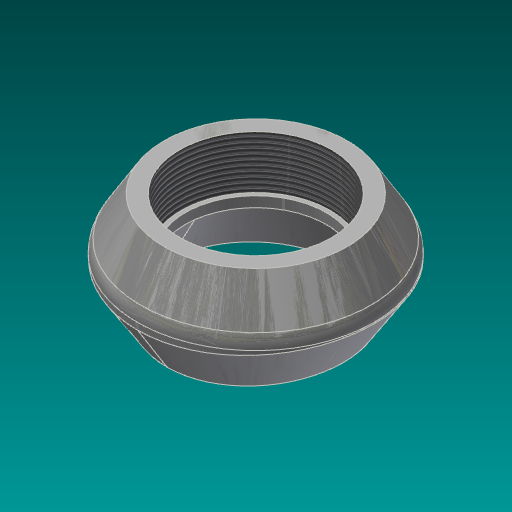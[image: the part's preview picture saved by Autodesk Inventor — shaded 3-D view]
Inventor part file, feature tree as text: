
AUTODESK INVENTOR PART (.ipt)
format: ipt  version: 2017.3 (Build 213256000, 256)  size: 448,512 bytes
history: native  units: mm (DEFAULTED — no unit token found)
features: other x8, sketch x5, plane x1, extrude x1, revolve x1, thread x1, sweep x1
ambient origin geometry x8: Origin, YZ Plane, XZ Plane, XY Plane, X Axis, Y Axis, Z Axis, Center Point
bodies: Solid1 (feature_tree)
feature tree (18):
  sketch  "Sketch1"  dims[d5=38.1mm d8=90.0deg]
  plane  "Work Plane1"
  sketch  "Sketch2"  dims[d9=0.0mm d10=898.525mm d11=10.0mm d12=0.0mm]
  extrude  "Extrusion1"  TaperAngle=90.0deg  [1 undecoded]
  revolve  "Revolution2"  [1 undecoded]
  thread  "Thread1"  [1 undecoded]
  other  "Work Point1"
  sweep  "Sweep1"
  other  "Work Axis3"
  other  "Work Point2"
  other  "Work Point3"
  sketch  "Sketch3"  dims[d45=8.810625mm d52=88.10625mm]
  sketch  "Sketch4"  dims[d54=1161.25625mm d77=68.1482mm d80=38.1mm d81=19.2151mm d83=56.55818mm d85=0.312398mm d86=90.0deg d91=52.5018mm d92=6.0mm d93=4.0mm d94=2.0mm d95=90.0deg d96=3.84302mm d97=0.0mm d102=10.0mm d103=0.0mm d106=19.05mm d107=487.3625mm d120=-449.2625mm d121=0.0mm d129=0.78232mm d130=0.78232mm d131=30.0deg d132=11.509375mm d133=0.0mm d134=0.0mm d135=90.0deg d136=0.0mm d137=90.0deg d138=65.0875mm d139=58.3692mm d140=0.0mm]
  other  "Work Axis2"
  sketch  "3D Sketch1"
  other  "Edges14"
  other  "Edges15"
  other  "Work Axis4"
note: 3 required parameter values undecoded (feature->parameter linkage not recoverable at this tier; creation-order binding heuristic only, values carry confidence <= 0.55)